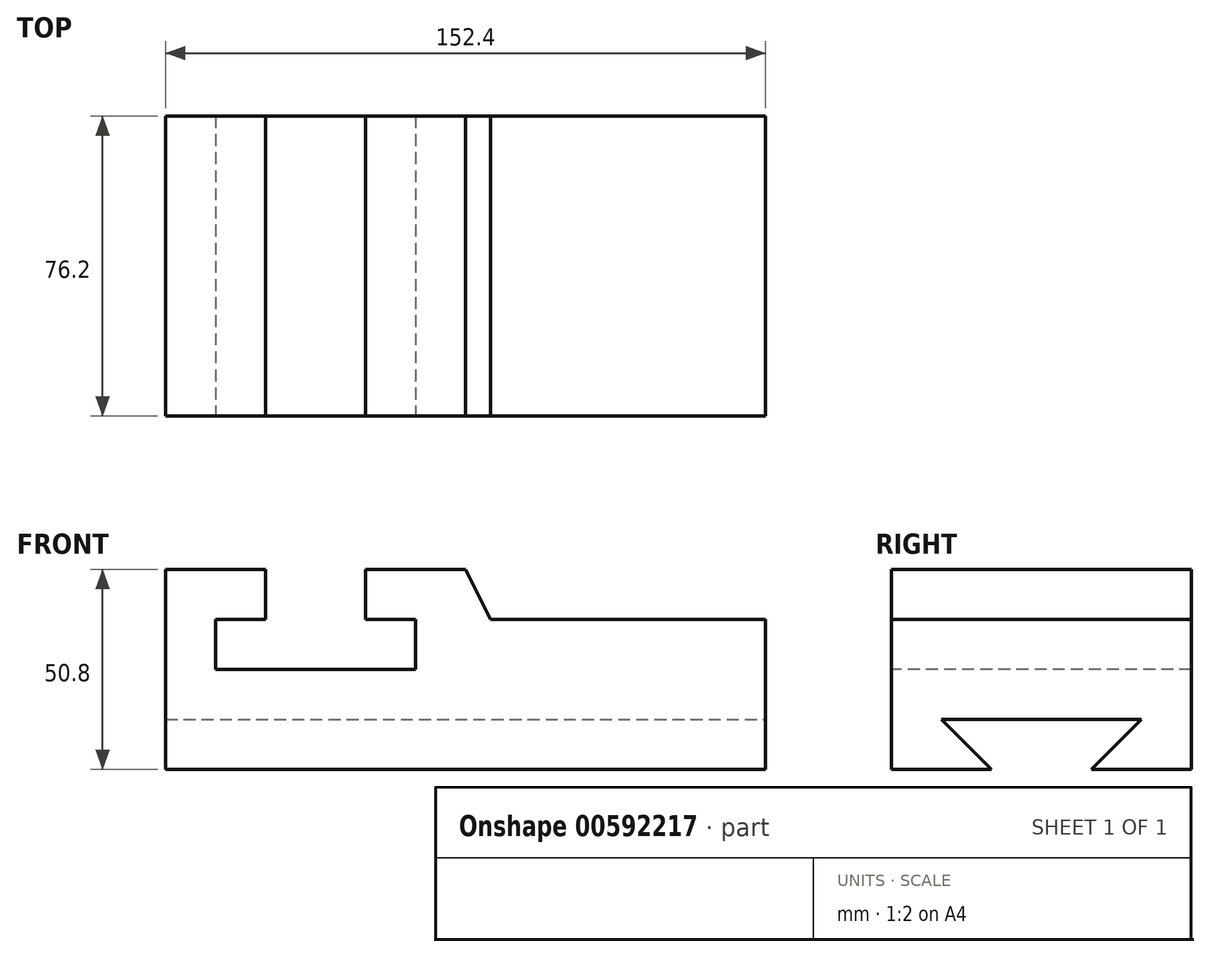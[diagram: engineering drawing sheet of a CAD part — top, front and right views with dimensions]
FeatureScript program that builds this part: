
annotation { "Feature Type Name" : "Feature", "Feature Type Description" : "" }
export const myFeature = defineFeature(function(context is Context, id is Id, definition is map)
    precondition{}
    {
        {
            var Q0;
            Q0=qCreatedBy(makeId("Front.planeOp"),FACE);
            var sketch = newSketch(context, id + "F0", { "sketchPlane" : qUnion([Q0])});
            skLineSegment(sketch, "E0.bottom", {"start": v(0, 0) * mm, "end": v(152.4, 0) * mm});
            skLineSegment(sketch, "E0.top", {"start": v(0, 50.8) * mm, "end": v(152.4, 50.8) * mm});
            skLineSegment(sketch, "E0.left", {"start": v(0, 0) * mm, "end": v(0, 50.8) * mm});
            skLineSegment(sketch, "E0.right", {"start": v(152.4, 0) * mm, "end": v(152.4, 50.8) * mm});
            skSolve(sketch);
        }
        {
            var Q0;
            Q0=makeQuery(id+"F0.imprint","IMPRINT",FACE,{"disambiguationData":[TD([[makeQuery(id+"F0.imprint","IMPRINT",EDGE,{"derivedFrom":sQuery(id+"F0.wireOp",EDGE,"E0.bottom")}),1.0]])]});
            extrude(context, id + "F1", {"entities" : qUnion([Q0]), "oppositeDirection" : true, "depth" : 76.2 * mm, "offsetDistance" : 25.4 * mm});
        }
        {
            var Q0;
            Q0=makeQuery(id+"F1.opExtrude","CAP_FACE",FACE,{"disambiguationData":[OSD([sQuery(id+"F0.wireOp",EDGE,"E0.bottom"),sQuery(id+"F0.wireOp",EDGE,"E0.top"),sQuery(id+"F0.wireOp",EDGE,"E0.left"),sQuery(id+"F0.wireOp",EDGE,"E0.right")])],"isStart":true});
            var sketch = newSketch(context, id + "F2", { "sketchPlane" : qUnion([Q0])});
            skLineSegment(sketch, "E1", {"start": v(0, 0) * mm, "end": v(0, 50.8) * mm});
            skLineSegment(sketch, "E2", {"start": v(0, 50.8) * mm, "end": v(25.4, 50.8) * mm});
            skLineSegment(sketch, "E3", {"start": v(25.4, 50.8) * mm, "end": v(25.4, 38.1) * mm});
            skLineSegment(sketch, "E4", {"start": v(25.4, 38.1) * mm, "end": v(12.7, 38.1) * mm});
            skLineSegment(sketch, "E5", {"start": v(12.7, 38.1) * mm, "end": v(12.7, 25.4) * mm});
            skLineSegment(sketch, "E6", {"start": v(12.7, 25.4) * mm, "end": v(63.5, 25.4) * mm});
            skLineSegment(sketch, "E7", {"start": v(63.5, 25.4) * mm, "end": v(63.5, 38.1) * mm});
            skLineSegment(sketch, "E8", {"start": v(63.5, 38.1) * mm, "end": v(50.8, 38.1) * mm});
            skLineSegment(sketch, "E9", {"start": v(50.8, 38.1) * mm, "end": v(50.8, 50.8) * mm});
            skLineSegment(sketch, "E10", {"start": v(50.8, 50.8) * mm, "end": v(152.4, 50.8) * mm});
            skLineSegment(sketch, "E11", {"start": v(152.4, 50.8) * mm, "end": v(152.4, 0) * mm});
            skLineSegment(sketch, "E12", {"start": v(152.4, 0) * mm, "end": v(0, 0) * mm});
            skSolve(sketch);
        }
        {
            var Q0;
            {var subQ0=sQuery(id+"F2.wireOp",EDGE,"E3");Q0=makeQuery(id+"F2.imprint","IMPRINT",FACE,{"disambiguationData":[TD([[makeQuery(id+"F2.imprint","IMPRINT",EDGE,{"derivedFrom":subQ0}),1.0]])]});}
            extrude(context, id + "F3", {"entities" : qUnion([Q0]), "operationType" : NewBodyOperationType.REMOVE, "oppositeDirection" : true, "depth" : 76.2 * mm, "offsetDistance" : 25.4 * mm});
        }
        {
            var Q0;
            Q0=makeQuery(id+"F1.opExtrude","SWEPT_FACE",FACE,{"disambiguationData":[OSD([sQuery(id+"F0.wireOp",EDGE,"E0.right")])]});
            var sketch = newSketch(context, id + "F4", { "sketchPlane" : qUnion([Q0])});
            skLineSegment(sketch, "E13", {"start": v(0, 0) * mm, "end": v(25.4, 0) * mm});
            skLineSegment(sketch, "E14", {"start": v(25.4, 0) * mm, "end": v(12.7, 12.7) * mm});
            skLineSegment(sketch, "E15", {"start": v(12.7, 12.7) * mm, "end": v(63.5, 12.7) * mm});
            skLineSegment(sketch, "E16", {"start": v(63.5, 12.7) * mm, "end": v(50.8, 0) * mm});
            skLineSegment(sketch, "E17", {"start": v(50.8, 0) * mm, "end": v(76.2, 0) * mm});
            skLineSegment(sketch, "E18", {"start": v(76.2, 0) * mm, "end": v(76.2, 50.8) * mm});
            skLineSegment(sketch, "E19", {"start": v(76.2, 50.8) * mm, "end": v(0, 50.8) * mm});
            skLineSegment(sketch, "E20", {"start": v(0, 50.8) * mm, "end": v(0, 0) * mm});
            skLineSegment(sketch, "E21", {"start": v(63.5, 12.7) * mm, "end": v(76.2, 12.7) * mm});
            skLineSegment(sketch, "E22", {"start": v(76.2, 12.7) * mm, "end": v(76.2, 0) * mm});
            skLineSegment(sketch, "E23", {"start": v(0, 0) * mm, "end": v(0, 12.7) * mm});
            skLineSegment(sketch, "E24", {"start": v(0, 12.7) * mm, "end": v(12.7, 12.7) * mm});
            skLineSegment(sketch, "E25", {"start": v(76.2, 0) * mm, "end": v(76.2, 12.7) * mm});
            skLineSegment(sketch, "E26", {"start": v(50.8, 0) * mm, "end": v(63.5, 12.7) * mm});
            skSolve(sketch);
        }
        {
            var Q0;
            Q0=makeQuery(id+"F1.opExtrude","CAP_FACE",FACE,{"disambiguationData":[OSD([sQuery(id+"F0.wireOp",EDGE,"E0.bottom"),sQuery(id+"F0.wireOp",EDGE,"E0.top"),sQuery(id+"F0.wireOp",EDGE,"E0.left"),sQuery(id+"F0.wireOp",EDGE,"E0.right")])],"isStart":true});
            var sketch = newSketch(context, id + "F5", { "sketchPlane" : qUnion([Q0])});
            skLineSegment(sketch, "E27", {"start": v(152.4, 50.8) * mm, "end": v(82.55, 50.8) * mm});
            skLineSegment(sketch, "E28", {"start": v(82.55, 50.8) * mm, "end": v(82.55, 38.1) * mm});
            skLineSegment(sketch, "E29", {"start": v(82.55, 38.1) * mm, "end": v(152.4, 38.1) * mm});
            skLineSegment(sketch, "E30", {"start": v(152.4, 38.1) * mm, "end": v(152.4, 50.8) * mm});
            skSolve(sketch);
        }
        {
            var Q0;
            Q0=makeQuery(id+"F5.imprint","IMPRINT",FACE,{"disambiguationData":[TD([[makeQuery(id+"F5.imprint","IMPRINT",EDGE,{"derivedFrom":sQuery(id+"F5.wireOp",EDGE,"E27")}),-1.0]])]});
            extrude(context, id + "F6", {"entities" : qUnion([Q0]), "operationType" : NewBodyOperationType.REMOVE, "oppositeDirection" : true, "depth" : 76.2 * mm, "offsetDistance" : 25.4 * mm});
        }
        {
            var Q0;
            Q0=makeQuery(id+"F1.opExtrude","CAP_FACE",FACE,{"disambiguationData":[OSD([sQuery(id+"F0.wireOp",EDGE,"E0.bottom"),sQuery(id+"F0.wireOp",EDGE,"E0.top"),sQuery(id+"F0.wireOp",EDGE,"E0.left"),sQuery(id+"F0.wireOp",EDGE,"E0.right")])],"isStart":true});
            var sketch = newSketch(context, id + "F7", { "sketchPlane" : qUnion([Q0])});
            skLineSegment(sketch, "E31", {"start": v(82.55, 38.1) * mm, "end": v(76.2, 50.8) * mm});
            skLineSegment(sketch, "E32", {"start": v(76.2, 50.8) * mm, "end": v(82.55, 50.8) * mm});
            skLineSegment(sketch, "E33", {"start": v(82.55, 50.8) * mm, "end": v(82.55, 38.1) * mm});
            skSolve(sketch);
        }
        {
            var Q0;
            Q0=makeQuery(id+"F7.imprint","IMPRINT",FACE,{"disambiguationData":[TD([[makeQuery(id+"F7.imprint","IMPRINT",EDGE,{"derivedFrom":sQuery(id+"F7.wireOp",EDGE,"E31")}),-1.0]])]});
            extrude(context, id + "F8", {"entities" : qUnion([Q0]), "operationType" : NewBodyOperationType.REMOVE, "oppositeDirection" : true, "depth" : 76.2 * mm, "offsetDistance" : 25.4 * mm});
        }
        {
            var Q0;
            {var subQ0=sQuery(id+"F4.wireOp",EDGE,"E14");Q0=makeQuery(id+"F4.imprint","IMPRINT",FACE,{"disambiguationData":[TD([[makeQuery(id+"F4.imprint","IMPRINT",EDGE,{"derivedFrom":subQ0}),-1.0]])]});}
            extrude(context, id + "F9", {"entities" : qUnion([Q0]), "operationType" : NewBodyOperationType.REMOVE, "oppositeDirection" : true, "depth" : 152.4 * mm, "offsetDistance" : 25.4 * mm});
        }
    });
